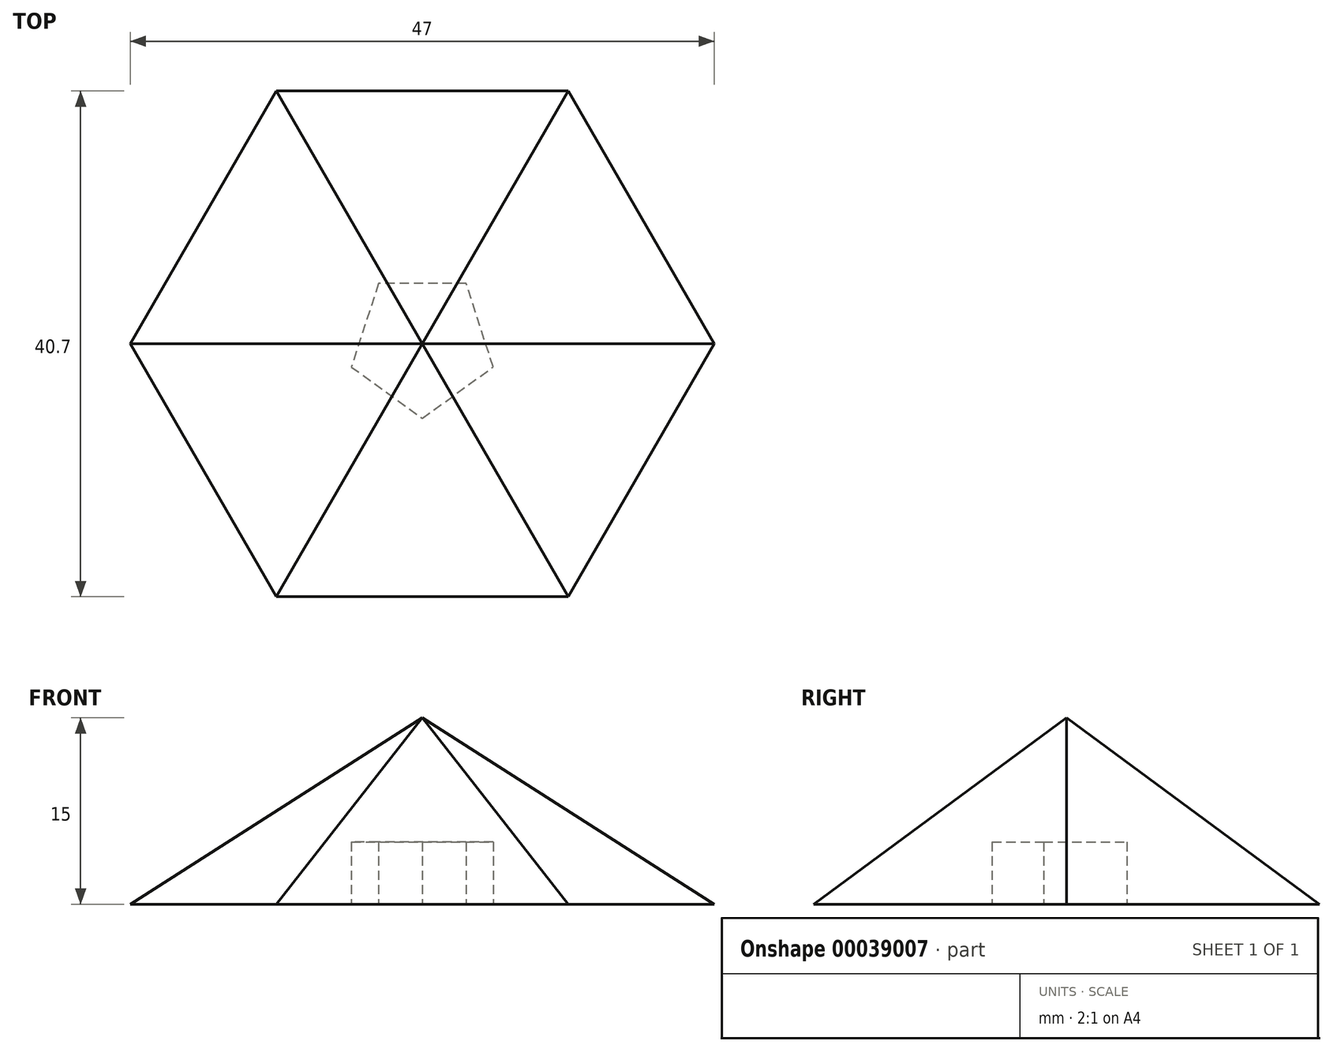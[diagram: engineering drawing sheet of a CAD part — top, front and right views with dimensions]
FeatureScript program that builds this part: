
annotation { "Feature Type Name" : "Feature", "Feature Type Description" : "" }
export const myFeature = defineFeature(function(context is Context, id is Id, definition is map)
    precondition{}
    {
        {
            var Q0;
            Q0=qCreatedBy(makeId("Top.planeOp"),FACE);
            var sketch = newSketch(context, id + "F0", { "sketchPlane" : qUnion([Q0])});
            skCircle(sketch, "E0.cCircle", {"center": v(0, 0) * mm, "radius": 20.35 * mm, "construction": true});
            skLineSegment(sketch, "E0.0", {"start": v(-11.75, 20.35) * mm, "end": v(11.75, 20.35) * mm});
            skLineSegment(sketch, "E0.1", {"start": v(11.75, 20.35) * mm, "end": v(23.5, 0) * mm});
            skLineSegment(sketch, "E0.2", {"start": v(23.5, 0) * mm, "end": v(11.75, -20.35) * mm});
            skLineSegment(sketch, "E0.3", {"start": v(11.75, -20.35) * mm, "end": v(-11.75, -20.35) * mm});
            skLineSegment(sketch, "E0.4", {"start": v(-11.75, -20.35) * mm, "end": v(-23.5, 0) * mm});
            skLineSegment(sketch, "E0.5", {"start": v(-23.5, 0) * mm, "end": v(-11.75, 20.35) * mm});
            skPoint(sketch, "E0.0.midPoint", {"position": v(0, 20.35) * mm});
            skSolve(sketch);
        }
        {
            var Q0;
            Q0=qCreatedBy(makeId("Top.planeOp"),FACE);
            cPlane(context, id + "F1", {"entities" : qUnion([Q0]), "cplaneType" : CPlaneType.OFFSET, "offset" : 15 * mm, "width" : 150 * mm, "height" : 150 * mm});
        }
        {
            var Q0;
            Q0=qCreatedBy(id+"F1.planeOp",FACE);
            var sketch = newSketch(context, id + "F2", { "sketchPlane" : qUnion([Q0])});
            skPoint(sketch, "E1", {"position": v(0, 0) * mm});
            skSolve(sketch);
        }
        {
            var Q0;
            Q0=sQuery(id+"F2.wireOp",VERTEX,"E1");
            var Q1;
            Q1=makeQuery(id+"F0.imprint","IMPRINT",FACE,{"disambiguationData":[TD([[makeQuery(id+"F0.imprint","IMPRINT",EDGE,{"derivedFrom":sQuery(id+"F0.wireOp",EDGE,"E0.0")}),-1.0]])]});
            loft(context, id + "F3", {"sheetProfilesArray" : [{ "sheetProfileEntities" : qUnion([Q0]) }, { "sheetProfileEntities" : qUnion([Q1]) }]});
        }
        {
            var Q0;
            Q0=makeQuery(id+"F3.opLoft","CAP_FACE",FACE,{"disambiguationData":[OSD([makeQuery(id+"F0.imprint","IMPRINT",FACE,{"disambiguationData":[TD([[makeQuery(id+"F0.imprint","IMPRINT",EDGE,{"derivedFrom":sQuery(id+"F0.wireOp",EDGE,"E0.0")}),-1.0]])]})])],"isStart":true});
            var sketch = newSketch(context, id + "F4", { "sketchPlane" : qUnion([Q0])});
            skCircle(sketch, "E2.cCircle", {"center": v(0, 0) * mm, "radius": 4.85 * mm, "construction": true});
            skLineSegment(sketch, "E2.0", {"start": v(3.53, -4.85) * mm, "end": v(-3.53, -4.85) * mm});
            skLineSegment(sketch, "E2.1", {"start": v(-3.53, -4.85) * mm, "end": v(-5.7, 1.85) * mm});
            skLineSegment(sketch, "E2.2", {"start": v(-5.7, 1.85) * mm, "end": v(0, 6) * mm});
            skLineSegment(sketch, "E2.3", {"start": v(0, 6) * mm, "end": v(5.7, 1.85) * mm});
            skLineSegment(sketch, "E2.4", {"start": v(5.7, 1.85) * mm, "end": v(3.53, -4.85) * mm});
            skPoint(sketch, "E2.0.midPoint", {"position": v(0, -4.85) * mm});
            skSolve(sketch);
        }
        {
            var Q0;
            Q0 = qSketchRegion(id + "F4", true);
            extrude(context, id + "F5", {"entities" : qUnion([Q0]), "operationType" : NewBodyOperationType.REMOVE, "oppositeDirection" : true, "depth" : 5 * mm});
        }
    });
